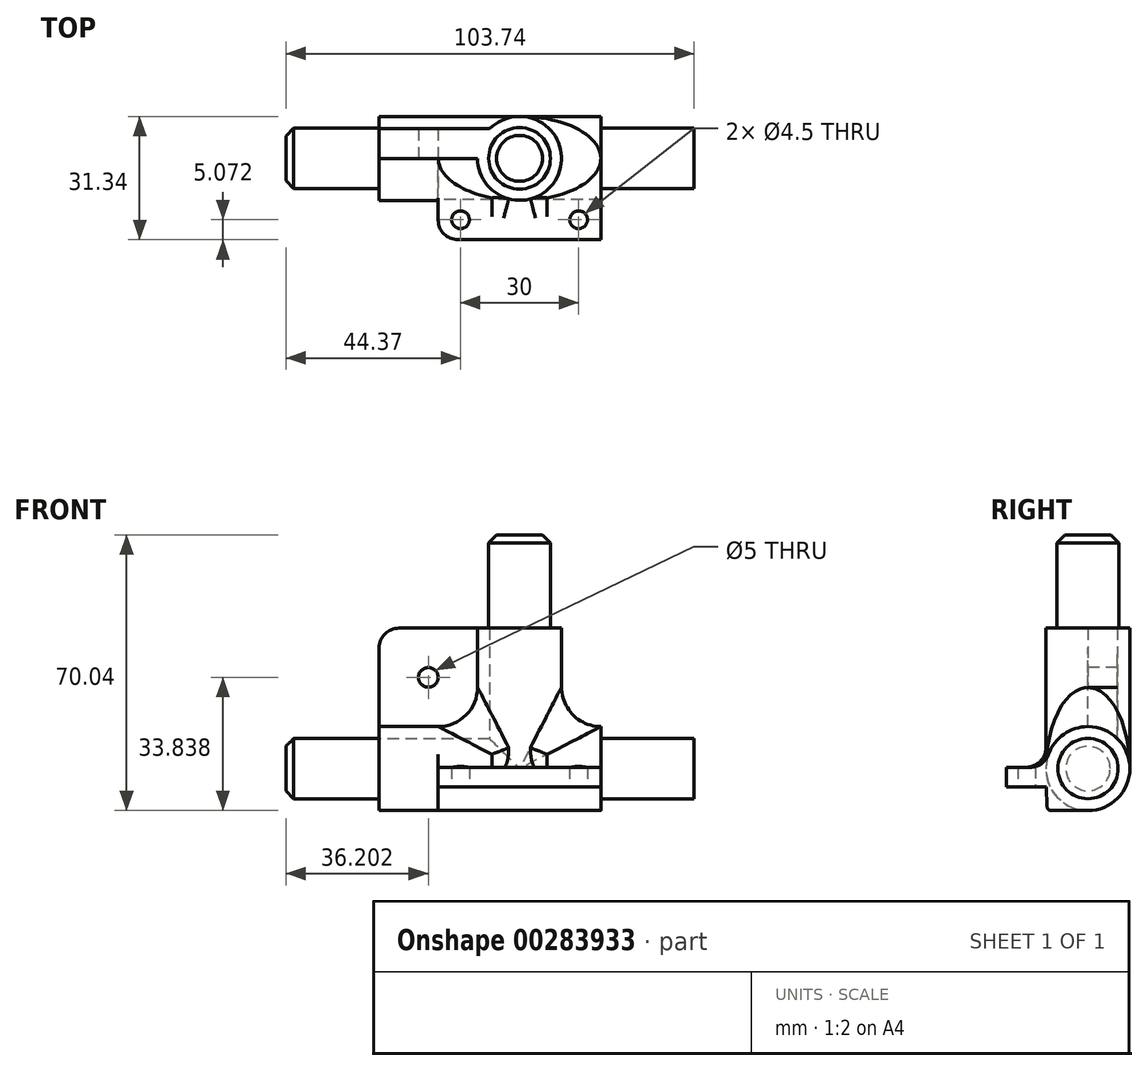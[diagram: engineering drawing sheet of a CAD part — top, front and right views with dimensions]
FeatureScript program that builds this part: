
annotation { "Feature Type Name" : "Feature", "Feature Type Description" : "" }
export const myFeature = defineFeature(function(context is Context, id is Id, definition is map)
    precondition{}
    {
        {
            var Q0;
            Q0=qCreatedBy(makeId("Right.planeOp"),FACE);
            var sketch = newSketch(context, id + "F0", { "sketchPlane" : qUnion([Q0])});
            skCircle(sketch, "E0", {"center": v(0, 0) * mm, "radius": 10.67 * mm});
            skSolve(sketch);
        }
        {
            var Q0;
            Q0=qSketchRegion(id+"F0",true);
            extrude(context, id + "F1", {"entities" : qUnion([Q0]), "endBound" : BoundingType.SYMMETRIC, "depth" : 21.34 * mm + 20 * mm});
        }
        {
            var Q0;
            Q0=makeQuery(id+"F1.opExtrude","CAP_FACE",FACE,{"disambiguationData":[OSD([sQuery(id+"F0.wireOp",EDGE,"E0")])],"isStart":false});
            var sketch = newSketch(context, id + "F2", { "sketchPlane" : qUnion([Q0])});
            skCircle(sketch, "E1", {"center": v(0, 0) * mm, "radius": 7.9 * mm});
            skSolve(sketch);
        }
        {
            var Q0;
            Q0=qSketchRegion(id+"F2",true);
            extrude(context, id + "F3", {"entities" : qUnion([Q0]), "operationType" : NewBodyOperationType.ADD, "depth" : 15.8 * mm * 1.5});
        }
        {
            var Q0;
            Q0=makeQuery(id+"F3.opExtrude","CAP_FACE",FACE,{"disambiguationData":[OSD([sQuery(id+"F2.wireOp",EDGE,"E1")])],"isStart":false});
            var sketch = newSketch(context, id + "F4", { "sketchPlane" : qUnion([Q0])});
            skCircle(sketch, "E2.0", {"center": v(0, 0) * mm, "radius": 7.9 * mm});
            skCircle(sketch, "E3", {"center": v(0, 0) * mm, "radius": 7.65 * mm});
            skSolve(sketch);
        }
        {
            var Q0;
            Q0=qSketchRegion(id+"F4",true);
            var Q1;
            Q1=makeQuery(id+"F1.opExtrude","CAP_FACE",FACE,{"disambiguationData":[OSD([sQuery(id+"F0.wireOp",EDGE,"E0")])],"isStart":false});
            extrude(context, id + "F5", {"entities" : qUnion([Q0]), "operationType" : NewBodyOperationType.REMOVE, "endBound" : BoundingType.UP_TO_SURFACE, "oppositeDirection" : true, "endBoundEntityFace" : qUnion([Q1]), "depth" : 25 * mm});
        }
        {
            var Q0;
            Q0=makeQuery(id+"F1.opExtrude","CAP_FACE",FACE,{"disambiguationData":[OSD([sQuery(id+"F0.wireOp",EDGE,"E0")])],"isStart":true});
            var sketch = newSketch(context, id + "F6", { "sketchPlane" : qUnion([Q0])});
            skCircle(sketch, "E4", {"center": v(0, 0) * mm, "radius": 7.65 * mm});
            skSolve(sketch);
        }
        {
            var Q0;
            Q0=qSketchRegion(id+"F6",true);
            extrude(context, id + "F7", {"entities" : qUnion([Q0]), "operationType" : NewBodyOperationType.ADD, "depth" : 15.8 * mm * 1.5 + 15 * mm});
        }
        {
            var Q0;
            Q0=qCreatedBy(makeId("Top.planeOp"),FACE);
            var sketch = newSketch(context, id + "F8", { "sketchPlane" : qUnion([Q0])});
            skCircle(sketch, "E5", {"center": v(0, 0) * mm, "radius": 10.67 * mm});
            skSolve(sketch);
        }
        {
            var Q0;
            Q0=qSketchRegion(id+"F8",true);
            extrude(context, id + "F9", {"entities" : qUnion([Q0]), "operationType" : NewBodyOperationType.ADD, "depth" : 21.34 * mm / 2 + 25 * mm});
        }
        {
            var Q0;
            Q0=makeQuery(id+"F9.opExtrude","CAP_FACE",FACE,{"disambiguationData":[OSD([sQuery(id+"F8.wireOp",EDGE,"E5")])],"isStart":false});
            var sketch = newSketch(context, id + "F10", { "sketchPlane" : qUnion([Q0])});
            skCircle(sketch, "E6", {"center": v(0, 0) * mm, "radius": 7.84 * mm});
            skSolve(sketch);
        }
        {
            var Q0;
            Q0=qSketchRegion(id+"F10",true);
            extrude(context, id + "F11", {"entities" : qUnion([Q0]), "operationType" : NewBodyOperationType.ADD, "depth" : 15.8 * mm * 1.5});
        }
        {
            var Q0;
            Q0=makeQuery(id+"F11.opExtrude","CAP_EDGE",EDGE,{"disambiguationData":[OSD([sQuery(id+"F10.wireOp",EDGE,"E6")])],"isStart":false});
            var Q1;
            Q1=makeQuery(id+"F5.boolean.opBoolean","COPY",EDGE,{"derivedFrom":makeQuery(id+"F5.opExtrude","CAP_EDGE",EDGE,{"disambiguationData":[OSD([sQuery(id+"F4.wireOp",EDGE,"E3")])],"isStart":true})});
            var Q2;
            Q2=makeQuery(id+"F7.opExtrude","CAP_EDGE",EDGE,{"disambiguationData":[OSD([sQuery(id+"F6.wireOp",EDGE,"E4")])],"isStart":false});
            chamfer(context, id + "F12", {"entities" : qUnion([Q0, Q1, Q2]), "width" : 2 * mm, "tangentPropagation" : true});
        }
        {
            var Q0;
            Q0=makeQuery(id+"F1.opExtrude","CAP_FACE",FACE,{"disambiguationData":[OSD([sQuery(id+"F0.wireOp",EDGE,"E0")])],"isStart":true});
            extrude(context, id + "F13", {"entities" : qUnion([Q0]), "operationType" : NewBodyOperationType.ADD, "depth" : 15 * mm});
        }
        {
            var Q0;
            Q0=qCreatedBy(makeId("Front.planeOp"),FACE);
            var sketch = newSketch(context, id + "F14", { "sketchPlane" : qUnion([Q0])});
            skLineSegment(sketch, "E7.0", {"start": v(-35.67, 10.67) * mm, "end": v(-35.67, -10.67) * mm, "construction": true});
            skLineSegment(sketch, "E7.1", {"start": v(-10.67, 35.67) * mm, "end": v(10.67, 35.67) * mm, "construction": true});
            skLineSegment(sketch, "E8.bottom", {"start": v(0, 0) * mm, "end": v(-35.67, 0) * mm});
            skLineSegment(sketch, "E8.top", {"start": v(0, 35.67) * mm, "end": v(-35.67, 35.67) * mm});
            skLineSegment(sketch, "E8.left", {"start": v(0, 0) * mm, "end": v(0, 35.67) * mm});
            skLineSegment(sketch, "E8.right", {"start": v(-35.67, 0) * mm, "end": v(-35.67, 35.67) * mm});
            skSolve(sketch);
        }
        {
            var Q0;
            Q0 = qSketchRegion(id + "F14", true);
            extrude(context, id + "F15", {"entities" : qUnion([Q0]), "operationType" : NewBodyOperationType.ADD, "oppositeDirection" : true, "depth" : 7.5 * mm});
        }
        {
            var Q0;
            Q0=makeQuery(id+"F15.opExtrude","SWEPT_EDGE",EDGE,{"disambiguationData":[OSD([sQuery(id+"F14.wireOp",EDGE,"E8.top"),sQuery(id+"F14.wireOp",EDGE,"E8.right")])]});
            fillet(context, id + "F16", {"entities" : qUnion([Q0]), "radius" : 5 * mm, "tangentPropagation" : true, "allowEdgeOverflow" : false});
        }
        {
            var Q0;
            Q0=makeQuery(id+"F15.opExtrude","CAP_FACE",FACE,{"disambiguationData":[OSD([sQuery(id+"F14.wireOp",EDGE,"E8.bottom"),sQuery(id+"F14.wireOp",EDGE,"E8.top"),sQuery(id+"F14.wireOp",EDGE,"E8.left"),sQuery(id+"F14.wireOp",EDGE,"E8.right")])],"isStart":true});
            var sketch = newSketch(context, id + "F17", { "sketchPlane" : qUnion([Q0])});
            skLineSegment(sketch, "E9", {"start": v(-23.17, 10.67) * mm, "end": v(-23.17, 35.67) * mm, "construction": true});
            skPoint(sketch, "E9.endSnap0", {"position": v(-20.67, 35.67) * mm});
            skCircle(sketch, "E10", {"center": v(-23.17, 23.17) * mm, "radius": 2.5 * mm});
            skSolve(sketch);
        }
        {
            var Q0;
            Q0 = qSketchRegion(id + "F17", true);
            extrude(context, id + "F18", {"entities" : qUnion([Q0]), "operationType" : NewBodyOperationType.REMOVE, "endBound" : BoundingType.THROUGH_ALL, "oppositeDirection" : true, "depth" : 25 * mm});
        }
        {
            var Q0;
            {var subQ0=sQuery(id+"F0.wireOp",EDGE,"E0");var subQ1=makeQuery(id+"F1.opExtrude","SWEPT_FACE",FACE,{"disambiguationData":[OSD([subQ0])]});var subQ2=makeQuery(id+"F9.opExtrude","SWEPT_FACE",FACE,{"disambiguationData":[OSD([sQuery(id+"F8.wireOp",EDGE,"E5")])]});Q0=makeQuery(id+"F15.boolean.opBoolean","SPLIT",EDGE,{"disambiguationData":[TD([makeQuery(id+"F15.opExtrude","CAP_FACE",FACE,{"disambiguationData":[OSD([sQuery(id+"F14.wireOp",EDGE,"E8.bottom"),sQuery(id+"F14.wireOp",EDGE,"E8.top"),sQuery(id+"F14.wireOp",EDGE,"E8.left"),sQuery(id+"F14.wireOp",EDGE,"E8.right")])],"isStart":true})])],"derivedFrom":makeQuery(id+"F9.boolean.opBoolean","INTERSECT",EDGE,{"disambiguationData":[OD(0.0)],"derivedFrom":[subQ1,subQ2]})});}
            var Q1;
            Q1=makeQuery(id+"F9.boolean.opBoolean","INTERSECT",EDGE,{"disambiguationData":[OD(1.0)],"derivedFrom":[makeQuery(id+"F1.opExtrude","SWEPT_FACE",FACE,{"disambiguationData":[OSD([sQuery(id+"F0.wireOp",EDGE,"E0")])]}),makeQuery(id+"F9.opExtrude","SWEPT_FACE",FACE,{"disambiguationData":[OSD([sQuery(id+"F8.wireOp",EDGE,"E5")])]})]});
            fillet(context, id + "F19", {"entities" : qUnion([Q0, Q1]), "radius" : 10 * mm, "tangentPropagation" : true, "allowEdgeOverflow" : false});
        }
        {
            var Q0;
            Q0=qCreatedBy(makeId("Right.planeOp"),FACE);
            var sketch = newSketch(context, id + "F20", { "sketchPlane" : qUnion([Q0])});
            skCircle(sketch, "E11.0", {"center": v(0, 0) * mm, "radius": 10.67 * mm, "construction": true});
            skLineSegment(sketch, "E12", {"start": v(0, 0) * mm, "end": v(0, -10.67) * mm, "construction": true});
            skLineSegment(sketch, "E13", {"start": v(0, -10.67) * mm, "end": v(-31.6, -10.67) * mm, "construction": true});
            skLineSegment(sketch, "E14.bottom", {"start": v(0, -4.67) * mm, "end": v(-20.67, -4.67) * mm});
            skLineSegment(sketch, "E14.top", {"start": v(0, 0.33) * mm, "end": v(-20.67, 0.33) * mm});
            skLineSegment(sketch, "E14.left", {"start": v(0, -4.67) * mm, "end": v(0, 0.33) * mm});
            skLineSegment(sketch, "E14.right", {"start": v(-20.67, -4.67) * mm, "end": v(-20.67, 0.33) * mm});
            skPoint(sketch, "E15", {"position": v(-10.67, 0) * mm});
            skSolve(sketch);
        }
        {
            var Q0;
            Q0 = qSketchRegion(id + "F20", true);
            var Q1;
            {var subQ0=sQuery(id+"F0.wireOp",EDGE,"E0");Q1=makeQuery(id+"F5.boolean.opBoolean","MERGE",FACE,{"derivedFrom":[makeQuery(id+"F1.opExtrude","CAP_FACE",FACE,{"disambiguationData":[OSD([subQ0])],"isStart":false}),makeQuery(id+"F5.opExtrude","CAP_FACE",FACE,{"disambiguationData":[OSD([subQ0])],"isStart":false})]});}
            var Q2;
            Q2=makeQuery(id+"F15.boolean.opBoolean","MERGE",FACE,{"derivedFrom":[makeQuery(id+"F13.opExtrude","CAP_FACE",FACE,{"disambiguationData":[OSD([sQuery(id+"F0.wireOp",EDGE,"E0")])],"isStart":false}),makeQuery(id+"F15.opExtrude","SWEPT_FACE",FACE,{"disambiguationData":[OSD([sQuery(id+"F14.wireOp",EDGE,"E8.right")])]})]});
            extrude(context, id + "F21", {"entities" : qUnion([Q0]), "operationType" : NewBodyOperationType.ADD, "endBound" : BoundingType.UP_TO_SURFACE, "endBoundEntityFace" : qUnion([Q1]), "depth" : 25 * mm, "hasSecondDirection" : true, "secondDirectionOppositeDirection" : true, "secondDirectionBoundEntityFace" : qUnion([Q2]), "secondDirectionDepth" : 10 * mm + 21.34 * mm / 2});
        }
        {
            var Q0;
            {var subQ0=sQuery(id+"F0.wireOp",EDGE,"E0");Q0=makeQuery(id+"F21.boolean.opBoolean","MERGE",FACE,{"derivedFrom":[makeQuery(id+"F5.boolean.opBoolean","MERGE",FACE,{"derivedFrom":[makeQuery(id+"F1.opExtrude","CAP_FACE",FACE,{"disambiguationData":[OSD([subQ0])],"isStart":false}),makeQuery(id+"F5.opExtrude","CAP_FACE",FACE,{"disambiguationData":[OSD([subQ0])],"isStart":false})]}),makeQuery(id+"F21.opExtrude","CAP_FACE",FACE,{"disambiguationData":[OSD([subQ0])],"isStart":false})]});}
            var sketch = newSketch(context, id + "F22", { "sketchPlane" : qUnion([Q0])});
            skLineSegment(sketch, "E16", {"start": v(-10.34, -10.67) * mm, "end": v(0, -10.67) * mm});
            skArc(sketch, "E17.0", {"start": v(-10.66, -0.33) * mm, "mid": v(-7.43, -7.66) * mm, "end": v(0, -10.67) * mm});
            skPoint(sketch, "E18.orphan", {"position": v(0, 10.67) * mm});
            skCircle(sketch, "E19", {"center": v(0, 0) * mm, "radius": 10.67 * mm, "construction": true});
            skLineSegment(sketch, "E20", {"start": v(0, 0) * mm, "end": v(-10.66, -0.33) * mm, "construction": true});
            skLineSegment(sketch, "E21", {"start": v(-10.66, -0.33) * mm, "end": v(-10.34, -10.67) * mm});
            skSolve(sketch);
        }
        {
            var Q0;
            Q0 = qSketchRegion(id + "F22", true);
            var Q1;
            Q1=makeQuery(id+"F21.opExtrude","CAP_FACE",FACE,{"disambiguationData":[OSD([sQuery(id+"F20.wireOp",EDGE,"E14.bottom"),sQuery(id+"F20.wireOp",EDGE,"E14.top"),sQuery(id+"F20.wireOp",EDGE,"E14.left"),sQuery(id+"F20.wireOp",EDGE,"E14.right")])],"isStart":true});
            extrude(context, id + "F23", {"entities" : qUnion([Q0]), "operationType" : NewBodyOperationType.ADD, "endBound" : BoundingType.UP_TO_SURFACE, "oppositeDirection" : true, "endBoundEntityFace" : qUnion([Q1]), "depth" : 25 * mm});
        }
        {
            var Q0;
            Q0=makeQuery(id+"F21.opExtrude","CAP_EDGE",EDGE,{"disambiguationData":[OSD([sQuery(id+"F20.wireOp",EDGE,"E14.right")])],"isStart":true});
            var Q1;
            {var subQ0=sQuery(id+"F0.wireOp",EDGE,"E0");Q1=makeQuery(id+"F21.opExtrude","TWEAK_EDGE",EDGE,{"derivedFrom":[makeQuery(id+"F5.boolean.opBoolean","MERGE",FACE,{"derivedFrom":[makeQuery(id+"F1.opExtrude","CAP_FACE",FACE,{"disambiguationData":[OSD([subQ0])],"isStart":false}),makeQuery(id+"F5.opExtrude","CAP_FACE",FACE,{"disambiguationData":[OSD([subQ0])],"isStart":false})]}),makeQuery(id+"F20.imprint","IMPRINT",EDGE,{"derivedFrom":sQuery(id+"F20.wireOp",EDGE,"E14.right")})]});}
            var Q2;
            {var subQ0=sQuery(id+"F0.wireOp",EDGE,"E0");Q2=makeQuery(id+"F21.boolean.opBoolean","INTERSECT",EDGE,{"disambiguationData":[OD(1.0)],"derivedFrom":[makeQuery(id+"F13.boolean.opBoolean","MERGE",FACE,{"derivedFrom":[makeQuery(id+"F1.opExtrude","SWEPT_FACE",FACE,{"disambiguationData":[OSD([subQ0])]}),makeQuery(id+"F13.opExtrude","SWEPT_FACE",FACE,{"disambiguationData":[OSD([subQ0])]})]}),makeQuery(id+"F21.opExtrude","SWEPT_FACE",FACE,{"disambiguationData":[OSD([sQuery(id+"F20.wireOp",EDGE,"E14.top")])]})]});}
            fillet(context, id + "F24", {"entities" : qUnion([Q0, Q1, Q2]), "radius" : 5 * mm, "tangentPropagation" : true, "allowEdgeOverflow" : false});
        }
        {
            var Q0;
            Q0=makeQuery(id+"F23.opExtrude","SWEPT_EDGE",EDGE,{"disambiguationData":[OSD([sQuery(id+"F22.wireOp",EDGE,"fKhVj6MA-809i-8CIR-IZio-RnfaeeeeRd3D"),sQuery(id+"F22.wireOp",EDGE,"E16")])]});
            fillet(context, id + "F25", {"entities" : qUnion([Q0]), "radius" : 1 * mm, "tangentPropagation" : true, "allowEdgeOverflow" : false});
        }
        {
            var Q0;
            Q0=makeQuery(id+"F21.opExtrude","SWEPT_FACE",FACE,{"disambiguationData":[OSD([sQuery(id+"F20.wireOp",EDGE,"E14.bottom")])]});
            var sketch = newSketch(context, id + "F26", { "sketchPlane" : qUnion([Q0])});
            skLineSegment(sketch, "E22", {"start": v(0, 20.67) * mm, "end": v(0, 10.53) * mm, "construction": true});
            skLineSegment(sketch, "E23", {"start": v(0, 15.6) * mm, "end": v(-15, 15.6) * mm, "construction": true});
            skCircle(sketch, "E24", {"center": v(-15, 15.6) * mm, "radius": 2.25 * mm});
            skCircle(sketch, "E25.MirrorC", {"center": v(15, 15.6) * mm, "radius": 2.25 * mm});
            skSolve(sketch);
        }
        {
            var Q0;
            Q0 = qSketchRegion(id + "F26", true);
            extrude(context, id + "F27", {"entities" : qUnion([Q0]), "operationType" : NewBodyOperationType.REMOVE, "endBound" : BoundingType.THROUGH_ALL, "oppositeDirection" : true, "depth" : 25 * mm});
        }
    });
